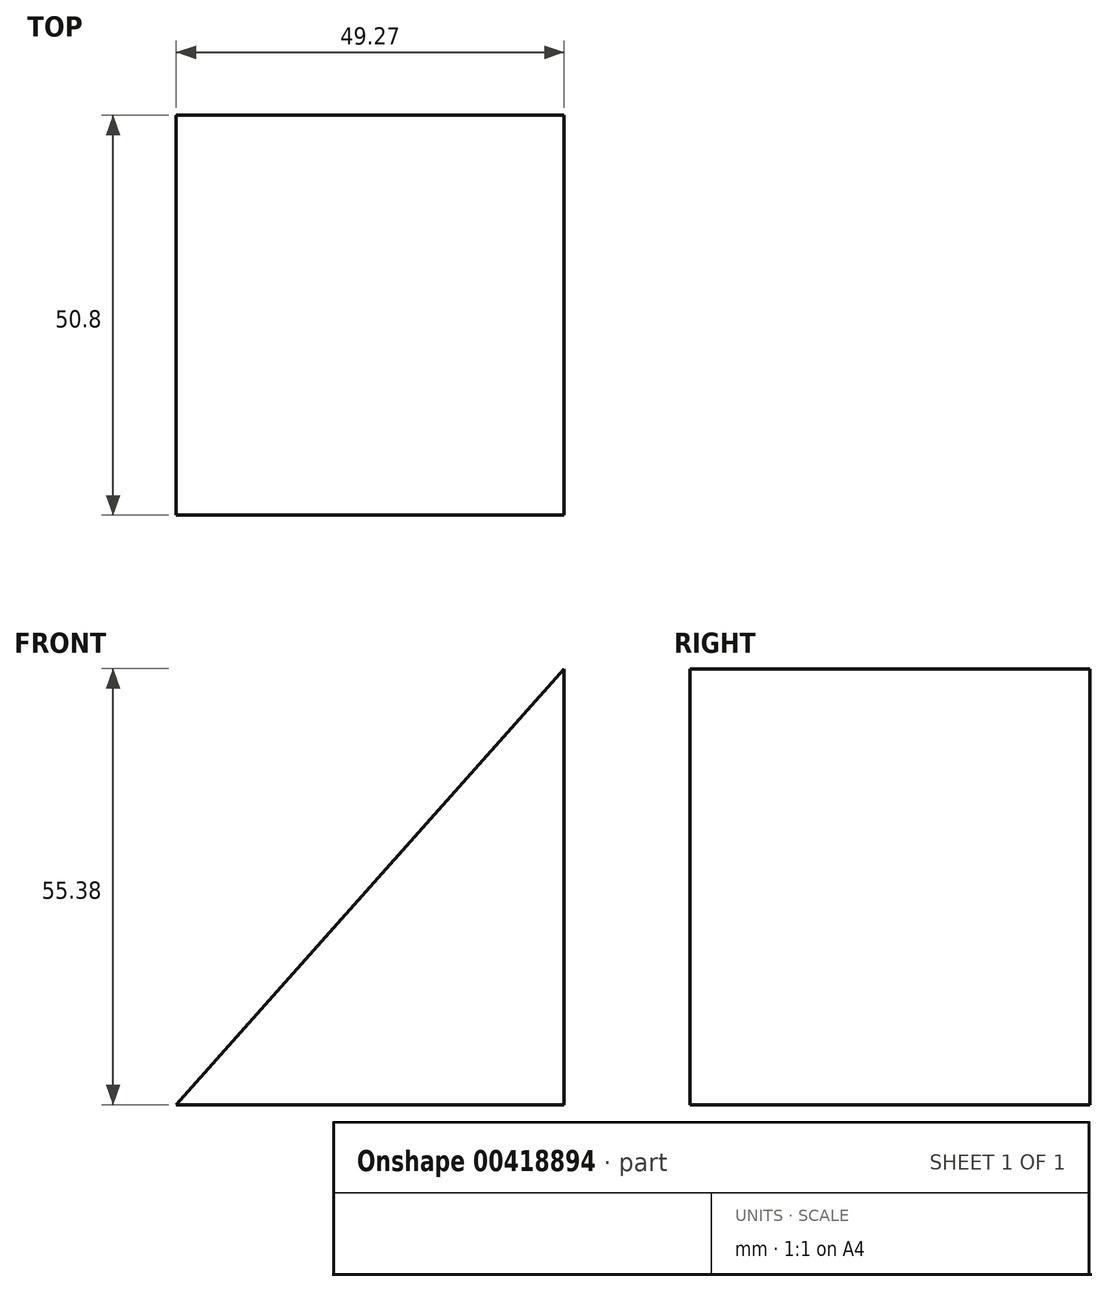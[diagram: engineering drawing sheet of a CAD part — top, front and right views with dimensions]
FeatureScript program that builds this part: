
annotation { "Feature Type Name" : "Feature", "Feature Type Description" : "" }
export const myFeature = defineFeature(function(context is Context, id is Id, definition is map)
    precondition{}
    {
        {
            var Q0;
            Q0=qCreatedBy(makeId("Front.planeOp"),FACE);
            var sketch = newSketch(context, id + "F0", { "sketchPlane" : qUnion([Q0])});
            skLineSegment(sketch, "E0", {"start": v(0, 55.38) * mm, "end": v(-49.27, 0) * mm});
            skLineSegment(sketch, "E1", {"start": v(-49.27, 0) * mm, "end": v(0, 0) * mm});
            skLineSegment(sketch, "E2", {"start": v(0, 0) * mm, "end": v(0, 55.38) * mm});
            skSolve(sketch);
        }
        {
            var Q0;
            Q0 = qSketchRegion(id + "F0", true);
            extrude(context, id + "F1", {"entities" : qUnion([Q0]), "depth" : 50.8 * mm});
        }
    });
